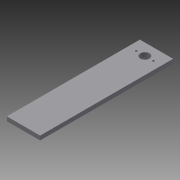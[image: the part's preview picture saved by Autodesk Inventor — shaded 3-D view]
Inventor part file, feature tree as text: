
AUTODESK INVENTOR PART (.ipt)
format: ipt  version: 2013 (Build 170138000, 138)  size: 81,920 bytes
history: native  units: in
note: dims shown in document units (in); Inventor stores cm internally (conversion verified against a paired STEP export)
features: extrude x1, sketch x1
ambient origin geometry x8: Origin, YZ Plane, XZ Plane, XY Plane, X Axis, Y Axis, Z Axis, Center Point
feature tree (2):
  extrude  "Extrusion2"  Depth=0.125in
  sketch  "Sketch2"  dims[d23=1.0in d24=4.0in d25=0.276in d26=0.35in d27=0.5in d28=0.06in d29=0.06in d30=0.518in d31=0.259in d32=0.35in d33=0.35in d34=1.0in d35=4.0in d36=0.276in d37=0.35in d38=0.06in d39=0.518in d40=0.125in d41=0.0in]
